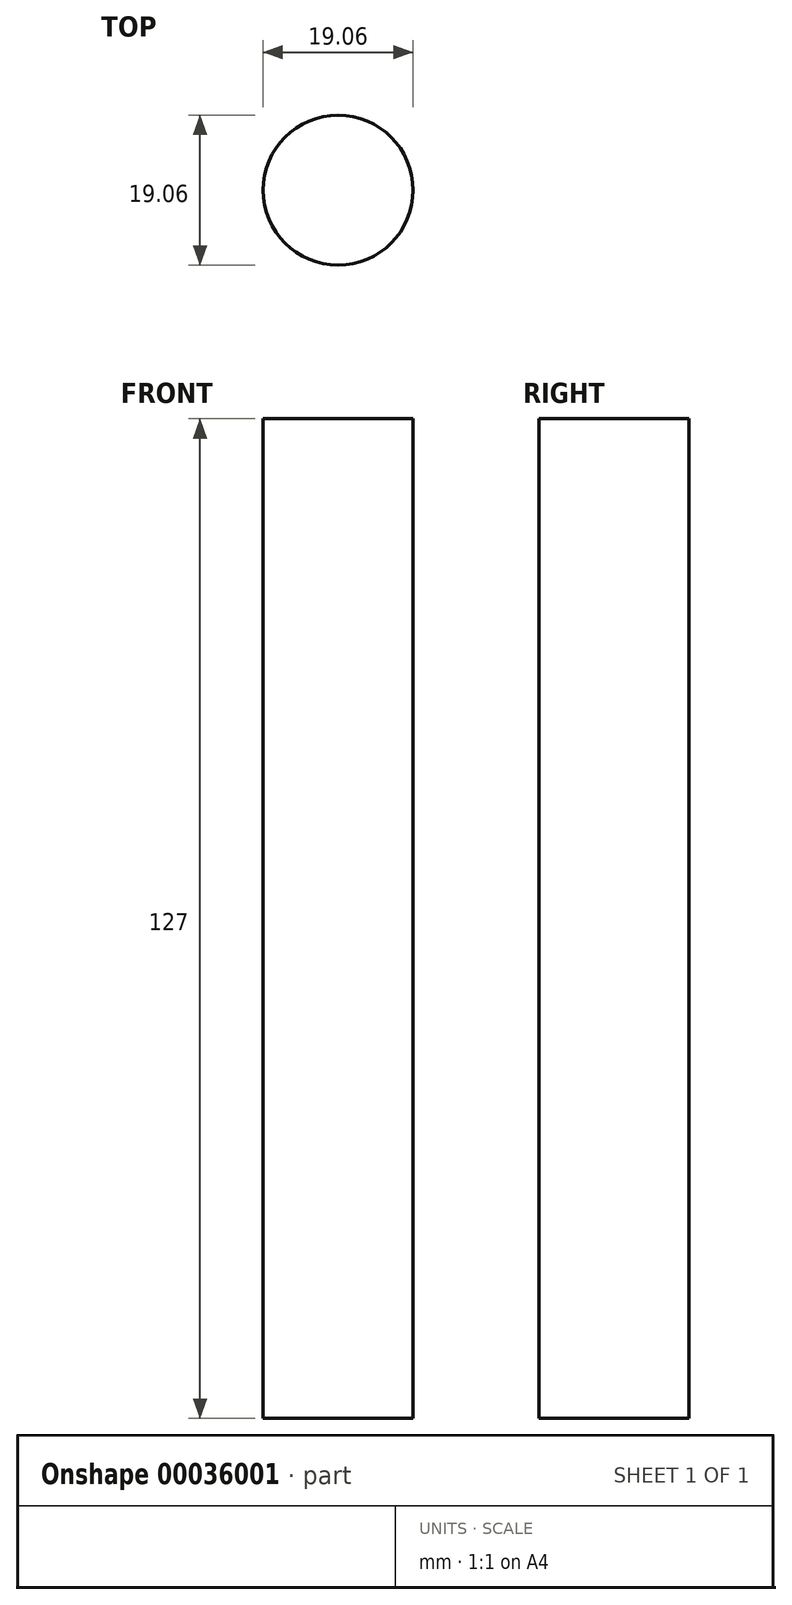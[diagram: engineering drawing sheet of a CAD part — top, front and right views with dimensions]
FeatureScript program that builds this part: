
annotation { "Feature Type Name" : "Feature", "Feature Type Description" : "" }
export const myFeature = defineFeature(function(context is Context, id is Id, definition is map)
    precondition{}
    {
        {
            var Q0;
            Q0=qCreatedBy(makeId("Top.planeOp"),FACE);
            var sketch = newSketch(context, id + "F0", { "sketchPlane" : qUnion([Q0])});
            skCircle(sketch, "E0", {"center": v(0, 0) * mm, "radius": 9.53 * mm});
            skSolve(sketch);
        }
        {
            var Q0;
            Q0 = qSketchRegion(id + "F0", true);
            extrude(context, id + "F1", {"entities" : qUnion([Q0]), "depth" : 127 * mm});
        }
    });
